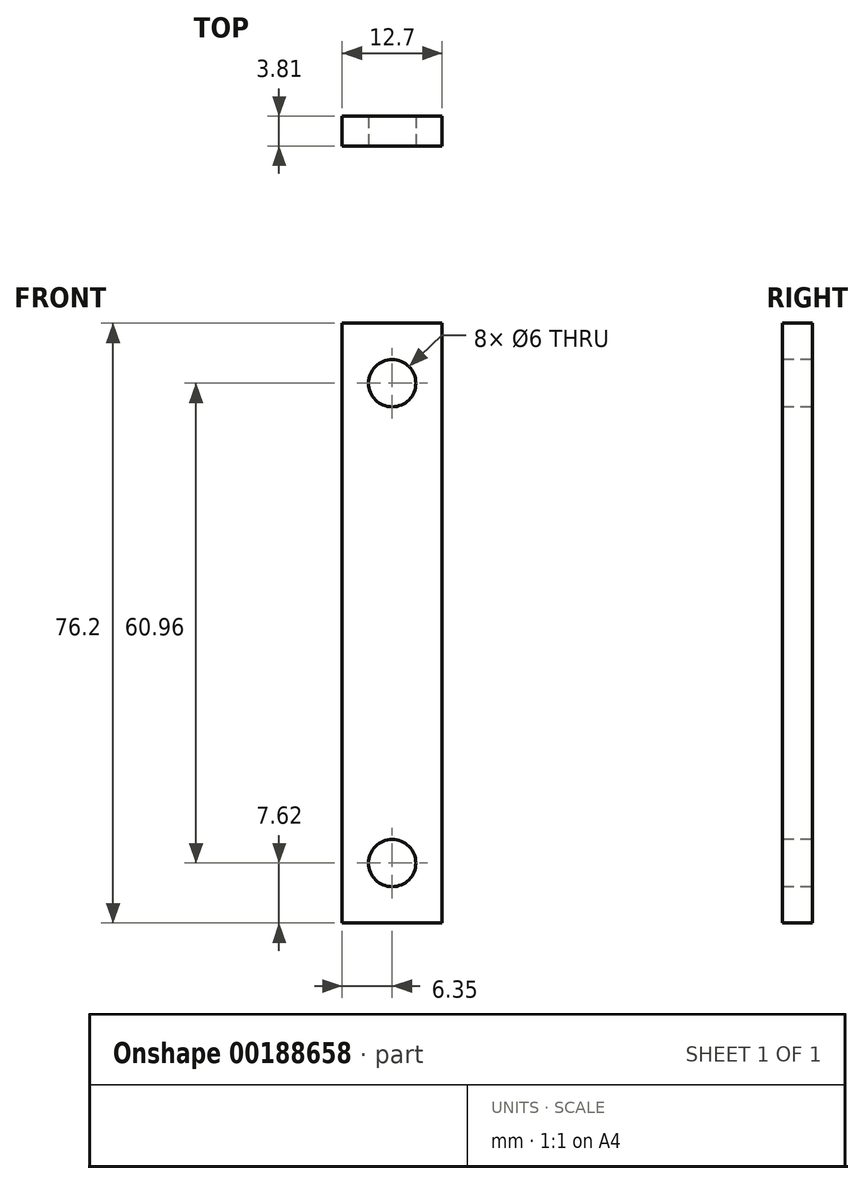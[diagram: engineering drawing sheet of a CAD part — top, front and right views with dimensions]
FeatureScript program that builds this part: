
annotation { "Feature Type Name" : "Feature", "Feature Type Description" : "" }
export const myFeature = defineFeature(function(context is Context, id is Id, definition is map)
    precondition{}
    {
        {
            var Q0;
            Q0=qCreatedBy(makeId("Front.planeOp"),FACE);
            var sketch = newSketch(context, id + "F0", { "sketchPlane" : qUnion([Q0])});
            skLineSegment(sketch, "E0.bottom", {"start": v(0, 0) * mm, "end": v(-12.7, 0) * mm});
            skLineSegment(sketch, "E0.top", {"start": v(0, -76.2) * mm, "end": v(-12.7, -76.2) * mm});
            skLineSegment(sketch, "E0.left", {"start": v(0, 0) * mm, "end": v(0, -76.2) * mm});
            skLineSegment(sketch, "E0.right", {"start": v(-12.7, 0) * mm, "end": v(-12.7, -76.2) * mm});
            skSolve(sketch);
        }
        {
            var Q0;
            Q0 = qSketchRegion(id + "F0", true);
            extrude(context, id + "F1", {"entities" : qUnion([Q0]), "depth" : 3.8 * mm});
        }
        {
            var Q0;
            Q0=makeQuery(id+"F1.opExtrude","CAP_FACE",FACE,{"disambiguationData":[OSD([sQuery(id+"F0.wireOp",EDGE,"E0.bottom"),sQuery(id+"F0.wireOp",EDGE,"E0.top"),sQuery(id+"F0.wireOp",EDGE,"E0.left"),sQuery(id+"F0.wireOp",EDGE,"E0.right")])],"isStart":false});
            var sketch = newSketch(context, id + "F2", { "sketchPlane" : qUnion([Q0])});
            skLineSegment(sketch, "E1", {"start": v(-6.35, 0) * mm, "end": v(-6.35, -76.2) * mm, "construction": true});
            skPoint(sketch, "E2", {"position": v(-6.35, -7.62) * mm});
            skPoint(sketch, "E3", {"position": v(-6.35, -68.58) * mm});
            skLineSegment(sketch, "E4", {"start": v(-12.7, -38.1) * mm, "end": v(0, -38.1) * mm, "construction": true});
            skSolve(sketch);
        }
        {
            var Q0;
            Q0=sQuery(id+"F2.wireOp",VERTEX,"E2");
            var Q1;
            Q1=sQuery(id+"F2.wireOp",VERTEX,"E3");
            var Q2;
            Q2=makeQuery(id+"F1.opExtrude","SWEPT_BODY",BODY,{"disambiguationData":[OSD([sQuery(id+"F0.wireOp",EDGE,"E0.bottom"),sQuery(id+"F0.wireOp",EDGE,"E0.top"),sQuery(id+"F0.wireOp",EDGE,"E0.left"),sQuery(id+"F0.wireOp",EDGE,"E0.right")])]});
            hole(context, id + "F3", {"style" : HoleStyle.SIMPLE, "endStyle" : HoleEndStyle.THROUGH, "standardTappedOrClearance" : lookupTablePath({ "standard" : "ISO", "size" : "6", "type" : "Drilled" }), "standardBlindInLast" : lookupTablePath({ "standard" : "ISO", "size" : "6", "type" : "Drilled" }), "holeDiameter" : 6 * mm, "startFromSketch" : true, "locations" : qUnion([Q0, Q1]), "scope" : qUnion([Q2]), "isTappedThrough" : true});
        }
    });
